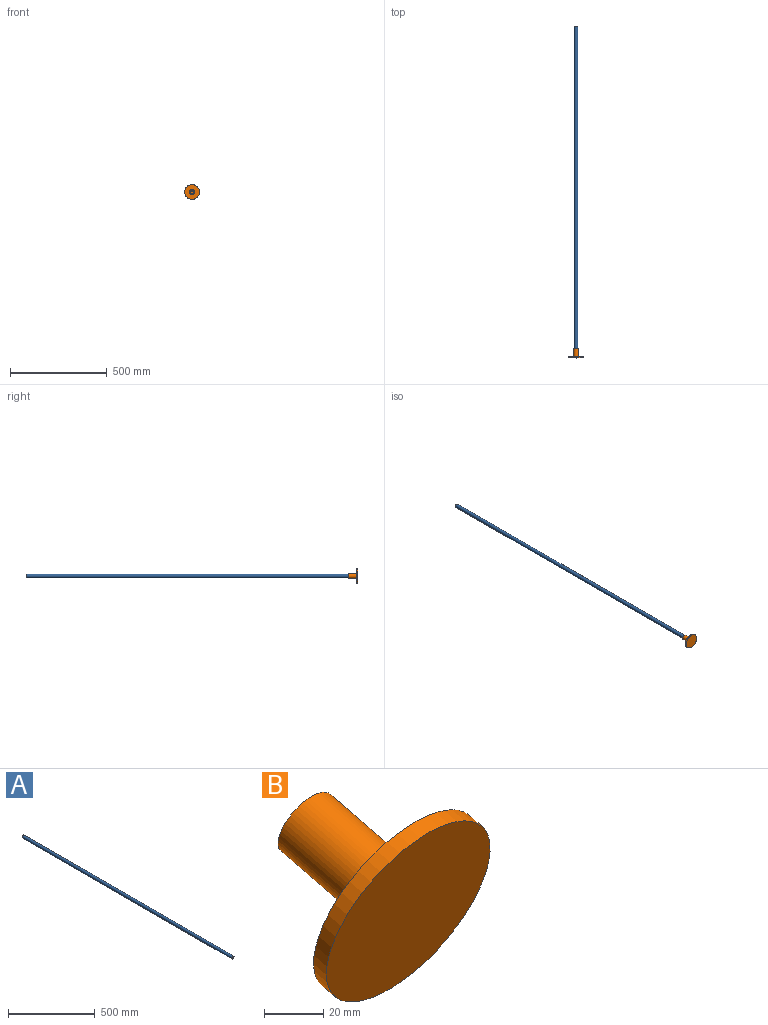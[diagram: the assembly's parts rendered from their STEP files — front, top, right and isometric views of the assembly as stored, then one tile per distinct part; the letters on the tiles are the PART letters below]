
ASSEMBLY  parts=2 mates=1
PART A: 4 faces, bbox 19.1x1712x19.1 mm
  f0: cylinder r=7.14mm len=1711.96mm, axis (0,1,0), area 76842.2mm2, adj f2,f3
  f1: cylinder r=9.53mm len=1711.96mm, axis (0,1,0), area 102456.3mm2, adj f2,f3
  f2: plane 19.05x19.05mm, normal (0,-1,0), area 124.7mm2, adj f0,f1
  f3: plane 19.05x19.05mm, normal (0,1,0), area 124.7mm2, adj f0,f1
PART B: 7 faces, bbox 76.2x61.6x75.5 mm
  f0: cylinder r=38.1mm len=76.2mm, axis (0,-0.97,-0.24), area 1520.1mm2, adj f1,f2
  f1: plane 76.2x73.94mm, normal (0,0.97,0.24), area 4053.7mm2, adj f0,f4
  f2: plane 76.2x73.94mm, normal (0,-0.97,-0.24), area 4560.4mm2, adj f0
  f3: cylinder r=9.53mm len=47.74mm, axis (0,-0.97,-0.24), area 2660.2mm2, adj f5,f6
  f4: cylinder r=12.7mm len=49.27mm, axis (0,-0.97,-0.24), area 3547mm2, adj f1,f5
  f5: plane 25.4x24.65mm, normal (0,0.97,0.24), area 221.7mm2, adj f3,f4
  f6: plane 19.05x18.48mm, normal (0,0.97,0.24), area 285mm2, adj f3
PLACE A t=(-230.3,-175.22,-63.39)mm
PLACE B rot(axis=(-1,0,0),14deg) t=(-230.3,-1037.55,-63.39)mm
MATE fastened B.f0 <-> A.f1  axis (0,1,0) through (-230.3,-1031.2,-63.39)mm
